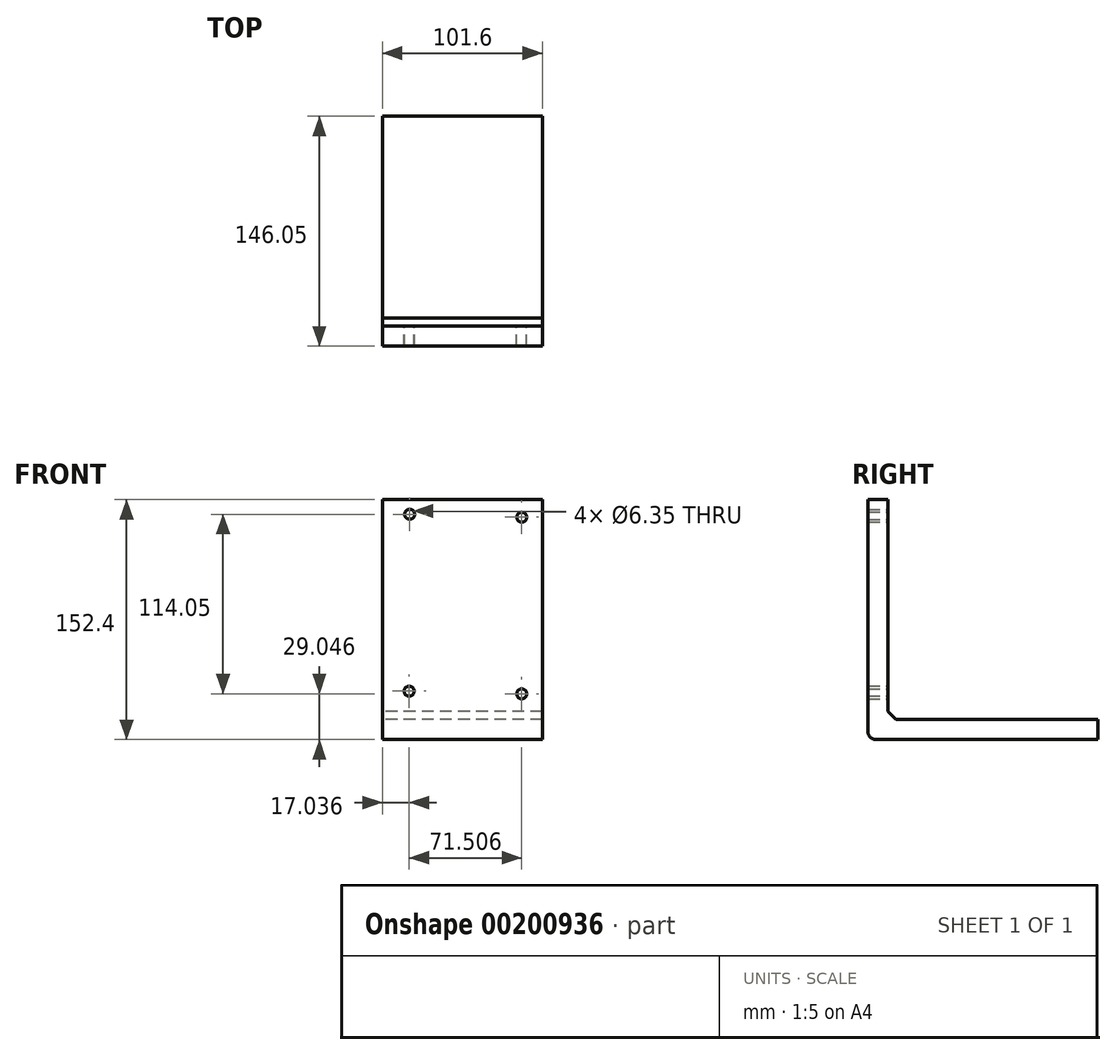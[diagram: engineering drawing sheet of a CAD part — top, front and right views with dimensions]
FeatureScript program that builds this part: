
annotation { "Feature Type Name" : "Feature", "Feature Type Description" : "" }
export const myFeature = defineFeature(function(context is Context, id is Id, definition is map)
    precondition{}
    {
        {
            var Q0;
            Q0=qCreatedBy(makeId("Front.planeOp"),FACE);
            var sketch = newSketch(context, id + "F0", { "sketchPlane" : qUnion([Q0])});
            skLineSegment(sketch, "E0.bottom", {"start": v(50.8, 76.2) * mm, "end": v(-50.8, 76.2) * mm});
            skLineSegment(sketch, "E0.top", {"start": v(50.8, -76.2) * mm, "end": v(-50.8, -76.2) * mm});
            skLineSegment(sketch, "E0.left", {"start": v(50.8, 76.2) * mm, "end": v(50.8, -76.2) * mm});
            skLineSegment(sketch, "E0.right", {"start": v(-50.8, 76.2) * mm, "end": v(-50.8, -76.2) * mm});
            skPoint(sketch, "E0.middle", {"position": v(0, 0) * mm});
            skSolve(sketch);
        }
        {
            var Q0;
            Q0=makeQuery(id+"F0.imprint","IMPRINT",FACE,{"disambiguationData":[TD([[makeQuery(id+"F0.imprint","IMPRINT",EDGE,{"derivedFrom":sQuery(id+"F0.wireOp",EDGE,"E0.bottom")}),1.0]])]});
            extrude(context, id + "F1", {"entities" : qUnion([Q0]), "endBound" : BoundingType.SYMMETRIC, "depth" : 12.7 * mm});
        }
        {
            var Q0;
            Q0=qCreatedBy(makeId("Right.planeOp"),FACE);
            var sketch = newSketch(context, id + "F2", { "sketchPlane" : qUnion([Q0])});
            skLineSegment(sketch, "E1.bottom", {"start": v(0, 0) * mm, "end": v(139.7, 0) * mm});
            skLineSegment(sketch, "E1.top", {"start": v(0, -76.2) * mm, "end": v(139.7, -76.2) * mm});
            skLineSegment(sketch, "E1.left", {"start": v(0, 0) * mm, "end": v(0, -76.2) * mm});
            skLineSegment(sketch, "E1.right", {"start": v(139.7, 0) * mm, "end": v(139.7, -76.2) * mm});
            skSolve(sketch);
        }
        {
            var Q0;
            Q0=makeQuery(id+"F2.imprint","IMPRINT",FACE,{"disambiguationData":[TD([[makeQuery(id+"F2.imprint","IMPRINT",EDGE,{"derivedFrom":sQuery(id+"F2.wireOp",EDGE,"E1.bottom")}),-1.0]])]});
            extrude(context, id + "F3", {"entities" : qUnion([Q0]), "operationType" : NewBodyOperationType.ADD, "endBound" : BoundingType.SYMMETRIC, "depth" : 101.6 * mm});
        }
        {
            var Q0;
            Q0=makeQuery(id+"F3.opExtrude","SWEPT_FACE",FACE,{"disambiguationData":[OSD([sQuery(id+"F2.wireOp",EDGE,"E1.bottom")])]});
            extrude(context, id + "F4", {"entities" : qUnion([Q0]), "operationType" : NewBodyOperationType.REMOVE, "oppositeDirection" : true, "depth" : 63.5 * mm});
        }
        {
            var Q0;
            Q0=makeQuery(id+"F4.boolean.opBoolean","COPY",EDGE,{"derivedFrom":makeQuery(id+"F4.opExtrude","CAP_EDGE",EDGE,{"disambiguationData":[OSD([sQuery(id+"F0.wireOp",EDGE,"E0.bottom"),sQuery(id+"F0.wireOp",EDGE,"E0.top"),sQuery(id+"F0.wireOp",EDGE,"E0.left"),sQuery(id+"F0.wireOp",EDGE,"E0.right"),sQuery(id+"F2.wireOp",EDGE,"E1.bottom")])],"isStart":false})});
            chamfer(context, id + "F5", {"entities" : qUnion([Q0]), "width" : 5.08 * mm, "tangentPropagation" : true});
        }
        {
            var Q0;
            Q0=makeQuery(id+"F1.opExtrude","CAP_EDGE",EDGE,{"disambiguationData":[OSD([sQuery(id+"F0.wireOp",EDGE,"E0.top")])],"isStart":false});
            fillet(context, id + "F6", {"entities" : qUnion([Q0]), "radius" : 5.08 * mm, "tangentPropagation" : true, "allowEdgeOverflow" : false});
        }
        {
            var Q0;
            {var subQ0=sQuery(id+"F0.wireOp",EDGE,"E0.right");var subQ1=sQuery(id+"F0.wireOp",EDGE,"E0.left");var subQ2=sQuery(id+"F0.wireOp",EDGE,"E0.top");var subQ3=sQuery(id+"F0.wireOp",EDGE,"E0.bottom");Q0=makeQuery(id+"F4.boolean.opBoolean","MERGE",FACE,{"derivedFrom":[makeQuery(id+"F1.opExtrude","CAP_FACE",FACE,{"disambiguationData":[OSD([subQ3,subQ2,subQ1,subQ0])],"isStart":true}),makeQuery(id+"F4.opExtrude","SWEPT_FACE",FACE,{"disambiguationData":[OSD([subQ3,subQ2,subQ1,subQ0,sQuery(id+"F2.wireOp",EDGE,"E1.bottom")])]})]});}
            var sketch = newSketch(context, id + "F7", { "sketchPlane" : qUnion([Q0])});
            skLineSegment(sketch, "E2", {"start": v(-50.8, 0) * mm, "end": v(50.8, 0) * mm, "construction": true});
            skLineSegment(sketch, "E3", {"start": v(-50.8, 76.2) * mm, "end": v(50.8, 76.2) * mm, "construction": true});
            skLineSegment(sketch, "E4", {"start": v(50.8, -58.42) * mm, "end": v(-50.8, -58.42) * mm, "construction": true});
            skCircle(sketch, "E5", {"center": v(-37.74, 65.04) * mm, "radius": 3.18 * mm});
            skPoint(sketch, "E5.first.point", {"position": v(-40.74, 66.1) * mm});
            skPoint(sketch, "E5.second.point", {"position": v(-35.83, 62.51) * mm});
            skPoint(sketch, "E5.third.point", {"position": v(-36.05, 67.73) * mm});
            skCircle(sketch, "E6", {"center": v(33.43, 66.9) * mm, "radius": 3.18 * mm});
            skPoint(sketch, "E6.first.point", {"position": v(30.37, 67.73) * mm});
            skPoint(sketch, "E6.second.point", {"position": v(36.5, 67.73) * mm});
            skPoint(sketch, "E6.third.point", {"position": v(35.75, 64.73) * mm});
            skCircle(sketch, "E7", {"center": v(33.76, -45.44) * mm, "radius": 3.18 * mm});
            skPoint(sketch, "E7.first.point", {"position": v(30.7, -44.65) * mm});
            skPoint(sketch, "E7.second.point", {"position": v(36.5, -43.82) * mm});
            skPoint(sketch, "E7.third.point", {"position": v(35.75, -47.92) * mm});
            skCircle(sketch, "E8", {"center": v(-37.73, -47.15) * mm, "radius": 3.18 * mm});
            skPoint(sketch, "E8.first.point", {"position": v(-40.74, -48.18) * mm});
            skPoint(sketch, "E8.second.point", {"position": v(-34.65, -47.92) * mm});
            skPoint(sketch, "E8.third.point", {"position": v(-38.1, -44) * mm});
            skSolve(sketch);
        }
        {
            var Q0;
            Q0=makeQuery(id+"F7.imprint","IMPRINT",FACE,{"disambiguationData":[TD([[makeQuery(id+"F7.imprint","IMPRINT",EDGE,{"derivedFrom":sQuery(id+"F7.wireOp",EDGE,"E5")}),1.0]])]});
            var Q1;
            Q1=makeQuery(id+"F7.imprint","IMPRINT",FACE,{"disambiguationData":[TD([[makeQuery(id+"F7.imprint","IMPRINT",EDGE,{"derivedFrom":sQuery(id+"F7.wireOp",EDGE,"E6")}),1.0]])]});
            var Q2;
            Q2=makeQuery(id+"F7.imprint","IMPRINT",FACE,{"disambiguationData":[TD([[makeQuery(id+"F7.imprint","IMPRINT",EDGE,{"derivedFrom":sQuery(id+"F7.wireOp",EDGE,"E7")}),1.0]])]});
            var Q3;
            Q3=makeQuery(id+"F7.imprint","IMPRINT",FACE,{"disambiguationData":[TD([[makeQuery(id+"F7.imprint","IMPRINT",EDGE,{"derivedFrom":sQuery(id+"F7.wireOp",EDGE,"E8")}),1.0]])]});
            extrude(context, id + "F8", {"entities" : qUnion([Q0, Q1, Q2, Q3]), "operationType" : NewBodyOperationType.REMOVE, "oppositeDirection" : true, "depth" : 12.7 * mm});
        }
    });
